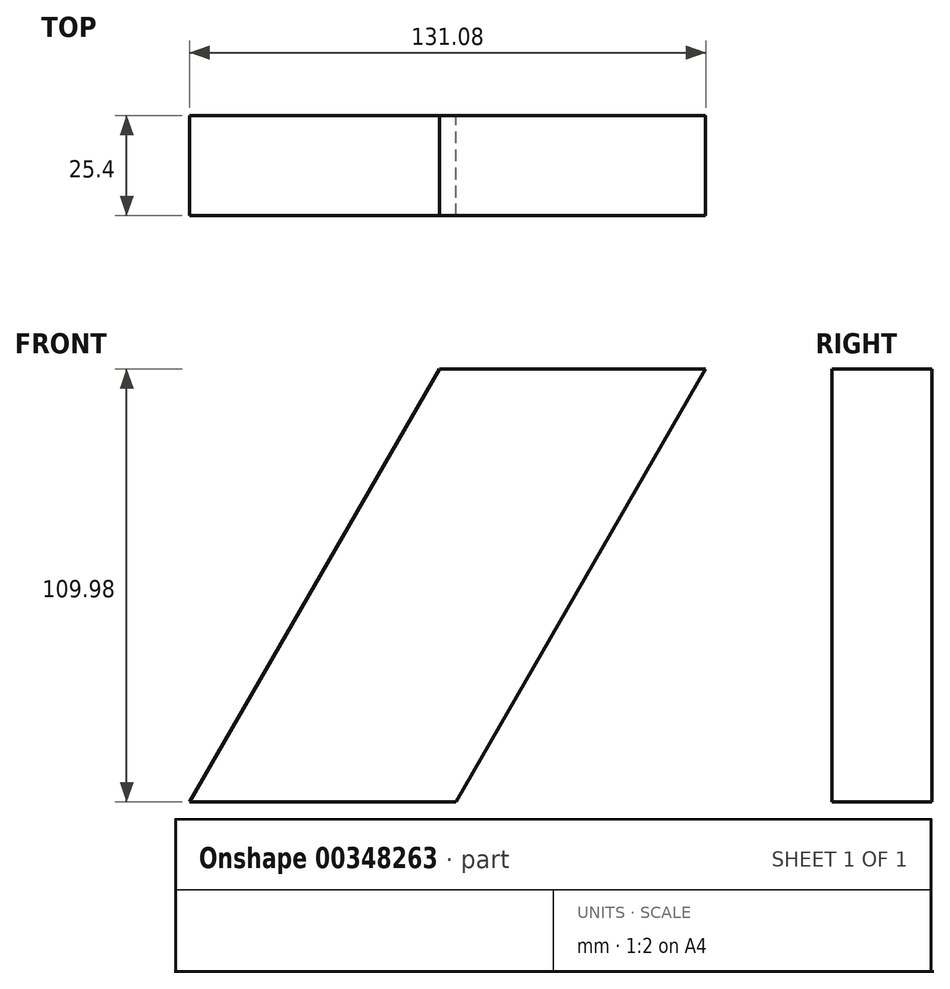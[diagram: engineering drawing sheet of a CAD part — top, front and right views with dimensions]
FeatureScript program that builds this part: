
annotation { "Feature Type Name" : "Feature", "Feature Type Description" : "" }
export const myFeature = defineFeature(function(context is Context, id is Id, definition is map)
    precondition{}
    {
        {
            var Q0;
            Q0=qCreatedBy(makeId("Front.planeOp"),FACE);
            var sketch = newSketch(context, id + "F0", { "sketchPlane" : qUnion([Q0])});
            skLineSegment(sketch, "E0.bottom", {"start": v(0, 56.7) * mm, "end": v(67.58, 56.7) * mm});
            skLineSegment(sketch, "E0.top", {"start": v(-63.5, -53.28) * mm, "end": v(4.08, -53.28) * mm});
            skLineSegment(sketch, "E0.left", {"start": v(0, 56.7) * mm, "end": v(-63.5, -53.28) * mm});
            skLineSegment(sketch, "E0.right", {"start": v(67.58, 56.7) * mm, "end": v(4.08, -53.28) * mm});
            skLineSegment(sketch, "E1", {"start": v(67.58, 56.7) * mm, "end": v(0, 0) * mm, "construction": true});
            skLineSegment(sketch, "E2", {"start": v(0, 0) * mm, "end": v(-63.5, -53.28) * mm, "construction": true});
            skSolve(sketch);
        }
        {
            var Q0;
            Q0 = qSketchRegion(id + "F0", true);
            extrude(context, id + "F1", {"entities" : qUnion([Q0]), "depth" : 25.4 * mm});
        }
    });
